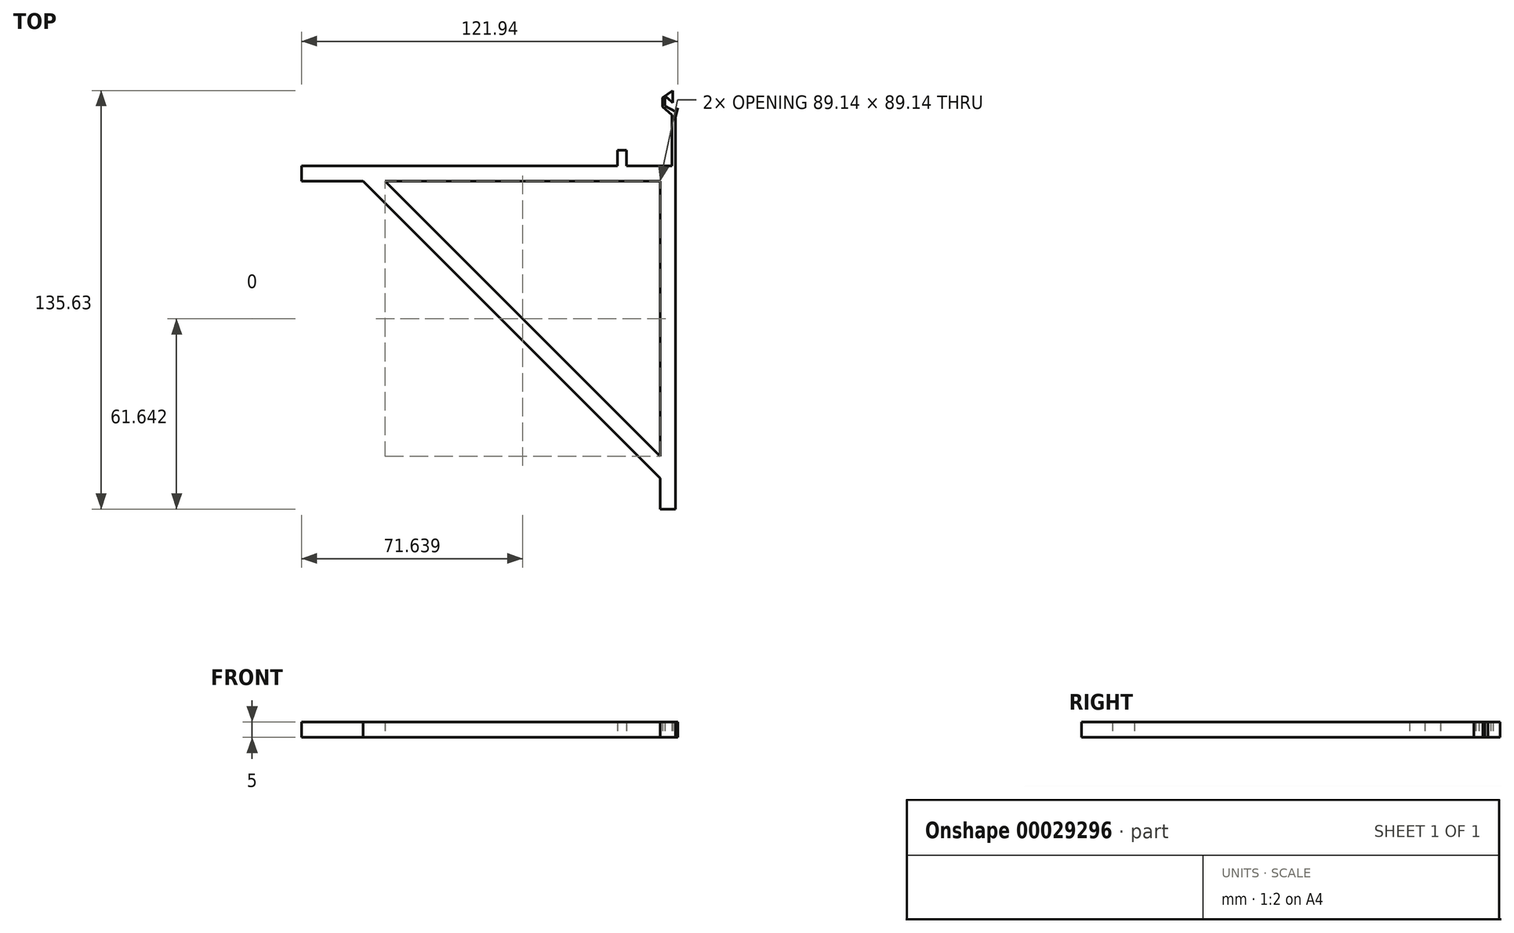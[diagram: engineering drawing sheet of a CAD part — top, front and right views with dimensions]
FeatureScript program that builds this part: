
annotation { "Feature Type Name" : "Feature", "Feature Type Description" : "" }
export const myFeature = defineFeature(function(context is Context, id is Id, definition is map)
    precondition{}
    {
        {
            var Q0;
            Q0=qCreatedBy(makeId("Top.planeOp"),FACE);
            var sketch = newSketch(context, id + "F0", { "sketchPlane" : qUnion([Q0])});
            skLineSegment(sketch, "E0", {"start": v(0, 0) * mm, "end": v(0, 4) * mm});
            skLineSegment(sketch, "E1", {"start": v(0, 4) * mm, "end": v(-3.28, 1.7) * mm});
            skLineSegment(sketch, "E2", {"start": v(-3.28, 1.7) * mm, "end": v(-3.28, -1.3) * mm});
            skLineSegment(sketch, "E3", {"start": v(0, 0) * mm, "end": v(-1.56, 1.56) * mm});
            skLineSegment(sketch, "E4", {"start": v(-2.5, 0.95) * mm, "end": v(-2.5, -1.05) * mm});
            skLineSegment(sketch, "E5", {"start": v(-2.5, -1.05) * mm, "end": v(1.01, -2.95) * mm});
            skLineSegment(sketch, "E6", {"start": v(1.01, -2.95) * mm, "end": v(1.73, -1.63) * mm});
            skLineSegment(sketch, "E7", {"start": v(1.73, -1.63) * mm, "end": v(1, -4.54) * mm});
            skLineSegment(sketch, "E8", {"start": v(-3.28, -1.3) * mm, "end": v(-0.21, -3.87) * mm});
            skLineSegment(sketch, "E9", {"start": v(1, -4.54) * mm, "end": v(1, -6.63) * mm});
            skPoint(sketch, "E10.end.orphan", {"position": v(-0.21, -5.62) * mm});
            skArc(sketch, "E11", {"start": v(-1.56, 1.56) * mm, "mid": v(-2.27, 1.63) * mm, "end": v(-2.5, 0.95) * mm});
            skLineSegment(sketch, "E12", {"start": v(-0.21, -20.42) * mm, "end": v(-14.87, -20.42) * mm});
            skLineSegment(sketch, "E13", {"start": v(-100.21, -25.42) * mm, "end": v(-4, -121.63) * mm});
            skLineSegment(sketch, "E14.0", {"start": v(-4, -25.42) * mm, "end": v(-93.14, -25.42) * mm});
            skLineSegment(sketch, "E15.0", {"start": v(-93.14, -25.42) * mm, "end": v(-4, -114.56) * mm});
            skLineSegment(sketch, "E16.0", {"start": v(-4, -114.56) * mm, "end": v(-4, -25.42) * mm});
            skLineSegment(sketch, "E17", {"start": v(-0.21, -3.87) * mm, "end": v(-0.21, -20.42) * mm});
            skLineSegment(sketch, "E18", {"start": v(1, -121.63) * mm, "end": v(1, -6.63) * mm});
            skLineSegment(sketch, "E19.left", {"start": v(-4, -121.63) * mm, "end": v(-4, -121.63) * mm});
            skLineSegment(sketch, "E19.right", {"start": v(1, -121.63) * mm, "end": v(1, -121.63) * mm});
            skLineSegment(sketch, "E20", {"start": v(1, -121.63) * mm, "end": v(1, -131.63) * mm});
            skLineSegment(sketch, "E21", {"start": v(-4, -121.63) * mm, "end": v(-4, -131.63) * mm});
            skLineSegment(sketch, "E22", {"start": v(-4, -131.63) * mm, "end": v(1, -131.63) * mm});
            skLineSegment(sketch, "E23", {"start": v(-100.21, -20.42) * mm, "end": v(-120.21, -20.42) * mm});
            skLineSegment(sketch, "E24", {"start": v(-100.21, -25.42) * mm, "end": v(-120.21, -25.42) * mm});
            skLineSegment(sketch, "E25", {"start": v(-120.21, -25.42) * mm, "end": v(-120.21, -20.42) * mm});
            skLineSegment(sketch, "E26", {"start": v(-14.87, -20.42) * mm, "end": v(-14.87, -15.4) * mm});
            skLineSegment(sketch, "E27", {"start": v(-14.87, -15.4) * mm, "end": v(-17.87, -15.4) * mm});
            skLineSegment(sketch, "E28", {"start": v(-17.87, -15.4) * mm, "end": v(-17.87, -20.42) * mm});
            skLineSegment(sketch, "E29.trimOffspring", {"start": v(-17.87, -20.42) * mm, "end": v(-100.21, -20.42) * mm});
            skSolve(sketch);
        }
        {
            var Q0;
            Q0 = qSketchRegion(id + "F0", true);
            extrude(context, id + "F1", {"entities" : qUnion([Q0]), "depth" : 5 * mm});
        }
    });
